# Revit family: SL500 Clean Room Surface Mount BP Narrow_GOTOVO
name_source: partatom
category: Doors
revit_build: Autodesk Revit Architecture 2014 (Build: 20130308_1515(x64)
units: mm (PartAtom-declared; Revit-internal decimal feet)

## types (4) — shared parameters
Analytic Construction = <None>
BIMobject category = Sliding Doors
Bottom Profile Option_01 = Slide panel : 0'4''
Bottom Profile Option_02 = Slide panel : 0'7''
Bottom Profile Option_03 = Slide panel : 0'10''
Bottom Profile Option_04 = Slide panel : 0'12''
Bottom_Profile_Height = Slide panel : 0'4''
Brass Polished Finish = Brass, Polished
Brass Satin Finish = Brass, Satin
Clear Anodized = Clear Anodized
Dark Bronze Anodized = Dark Bronze Anodized
Date of publishing = 2015-02-23
Depth = 0.00
Disclaimer = Consult product specification for sensors to comply with ANSI A156.10.
Edition number = 1
Frame Material = Clear Anodized
Function = Interior
Glass = Glass
Glass Type = Glass Type : 1/4''
Height = 7' - 0"
IFC Classification = Door
Leaf Height = 6' - 11 3/4"
Manufacturer name = Besam-North America
Material main = Aluminium
NBS Reference Code = 25-30-20-77
NBS Reference Description = Sliding Doorset Systems
Nominal height = 0.00
Nominal width = 0.00
Overall Frame Height = 7' - 7"
Product SKU = SL500_Clnrm_SM
Product data url = http://besam-na.bimobject.com
Product family = Sliding
Product group = Clean Room
QR code = http://besam-na.bimobject.com
Rough Height = 7' - 0"
Rubber = Rubber, Black
Stainless Steel Polished Finish = Stainless Steel, Polished
Stainless Steel Satin Finish = Stainless Steel, Satin
UNSPSC Code = 301715
Uniclass 1.4 Code = L4133
Uniclass 1.4 Description = Sliding
Uniclass 2.0 Code = SS-25-30-20-77
Uniclass 2.0 Description = Sliding Doorset Systems
Wall Closure = By host
Weight Net (Kg) = 0

## per-type parameters (varying)
| type | Leaf Width | Overall Frame Width | Rough Width | Width |
| 43 1/2'' | 2' - 0 3/8" | 8' - 0" | 3' - 7 1/2" | 3' - 7 1/2" |
| 72'' | 3' - 2 5/8" | 12' - 9" | 6' - 0" | 6' - 0" |
| 84'' | 3' - 8 5/8" | 14' - 9" | 7' - 0" | 7' - 0" |
| 96'' | 4' - 2 5/8" | 16' - 9" | 8' - 0" | 8' - 0" |

## geometry (parser evidence)
native form markers: Blend x4, Sweep x22
no freeform markers — native parametric forms only
